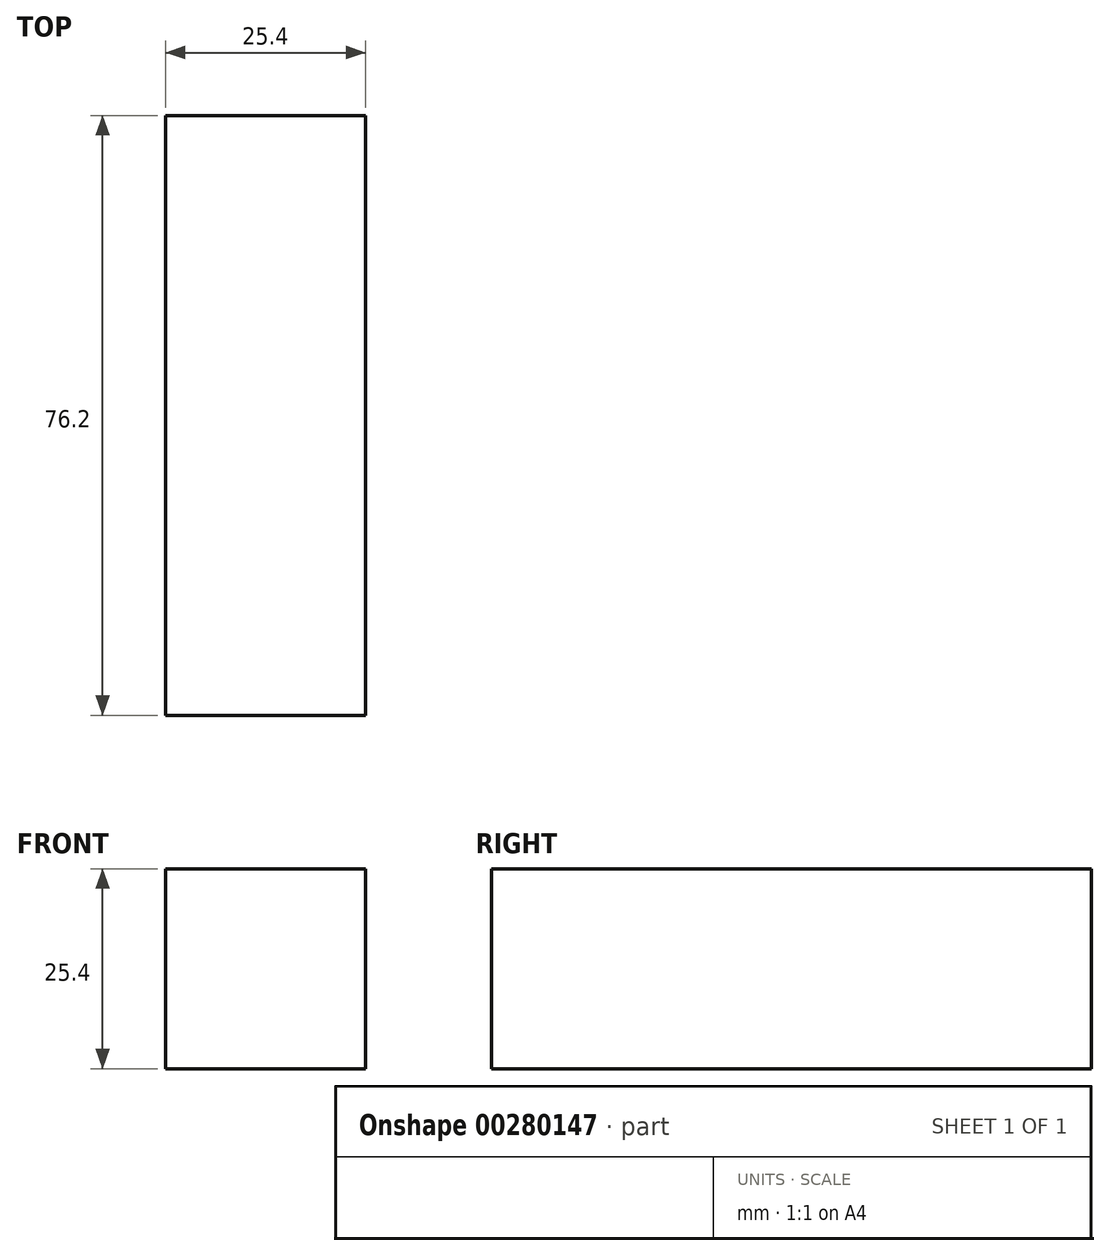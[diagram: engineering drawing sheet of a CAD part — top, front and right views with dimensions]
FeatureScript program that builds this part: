
annotation { "Feature Type Name" : "Feature", "Feature Type Description" : "" }
export const myFeature = defineFeature(function(context is Context, id is Id, definition is map)
    precondition{}
    {
        {
            var Q0;
            Q0=qCreatedBy(makeId("Front.planeOp"),FACE);
            var sketch = newSketch(context, id + "F0", { "sketchPlane" : qUnion([Q0])});
            skLineSegment(sketch, "E0.bottom", {"start": v(-41.7, 36.4) * mm, "end": v(-16.3, 36.4) * mm});
            skLineSegment(sketch, "E0.top", {"start": v(-41.7, 11) * mm, "end": v(-16.3, 11) * mm});
            skLineSegment(sketch, "E0.left", {"start": v(-41.7, 36.4) * mm, "end": v(-41.7, 11) * mm});
            skLineSegment(sketch, "E0.right", {"start": v(-16.3, 36.4) * mm, "end": v(-16.3, 11) * mm});
            skSolve(sketch);
        }
        {
            var Q0;
            Q0=makeQuery(id+"F0.imprint","IMPRINT",FACE,{"disambiguationData":[TD([[makeQuery(id+"F0.imprint","IMPRINT",EDGE,{"derivedFrom":sQuery(id+"F0.wireOp",EDGE,"E0.bottom")}),-1.0]])]});
            extrude(context, id + "F1", {"entities" : qUnion([Q0]), "depth" : 76.2 * mm});
        }
    });
